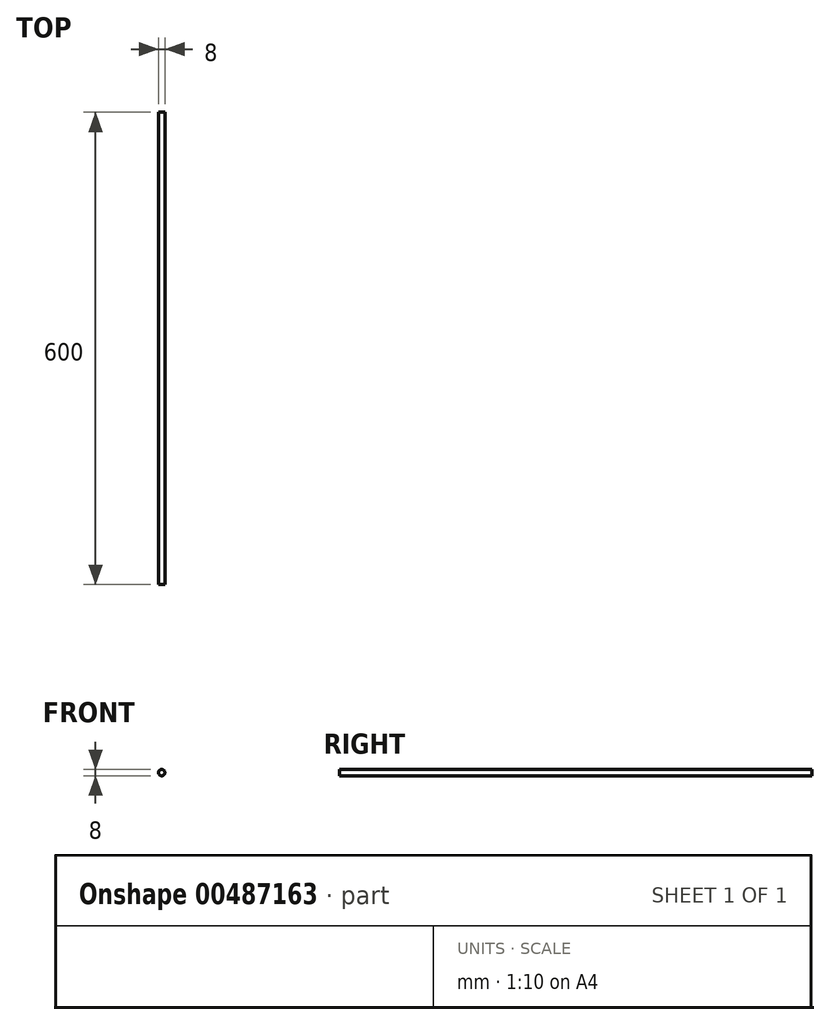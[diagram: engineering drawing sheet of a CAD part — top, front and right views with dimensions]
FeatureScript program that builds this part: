
annotation { "Feature Type Name" : "Feature", "Feature Type Description" : "" }
export const myFeature = defineFeature(function(context is Context, id is Id, definition is map)
    precondition{}
    {
        {
            var Q0;
            Q0=qCreatedBy(makeId("Front.planeOp"),FACE);
            var sketch = newSketch(context, id + "F0", { "sketchPlane" : qUnion([Q0])});
            skCircle(sketch, "E0", {"center": v(0, 0) * mm, "radius": 4 * mm});
            skSolve(sketch);
        }
        {
            var Q0;
            Q0 = qSketchRegion(id + "F0", true);
            extrude(context, id + "F1", {"entities" : qUnion([Q0]), "depth" : 300 * mm, "hasSecondDirection" : true, "secondDirectionOppositeDirection" : true, "secondDirectionDepth" : 300 * mm});
        }
    });
